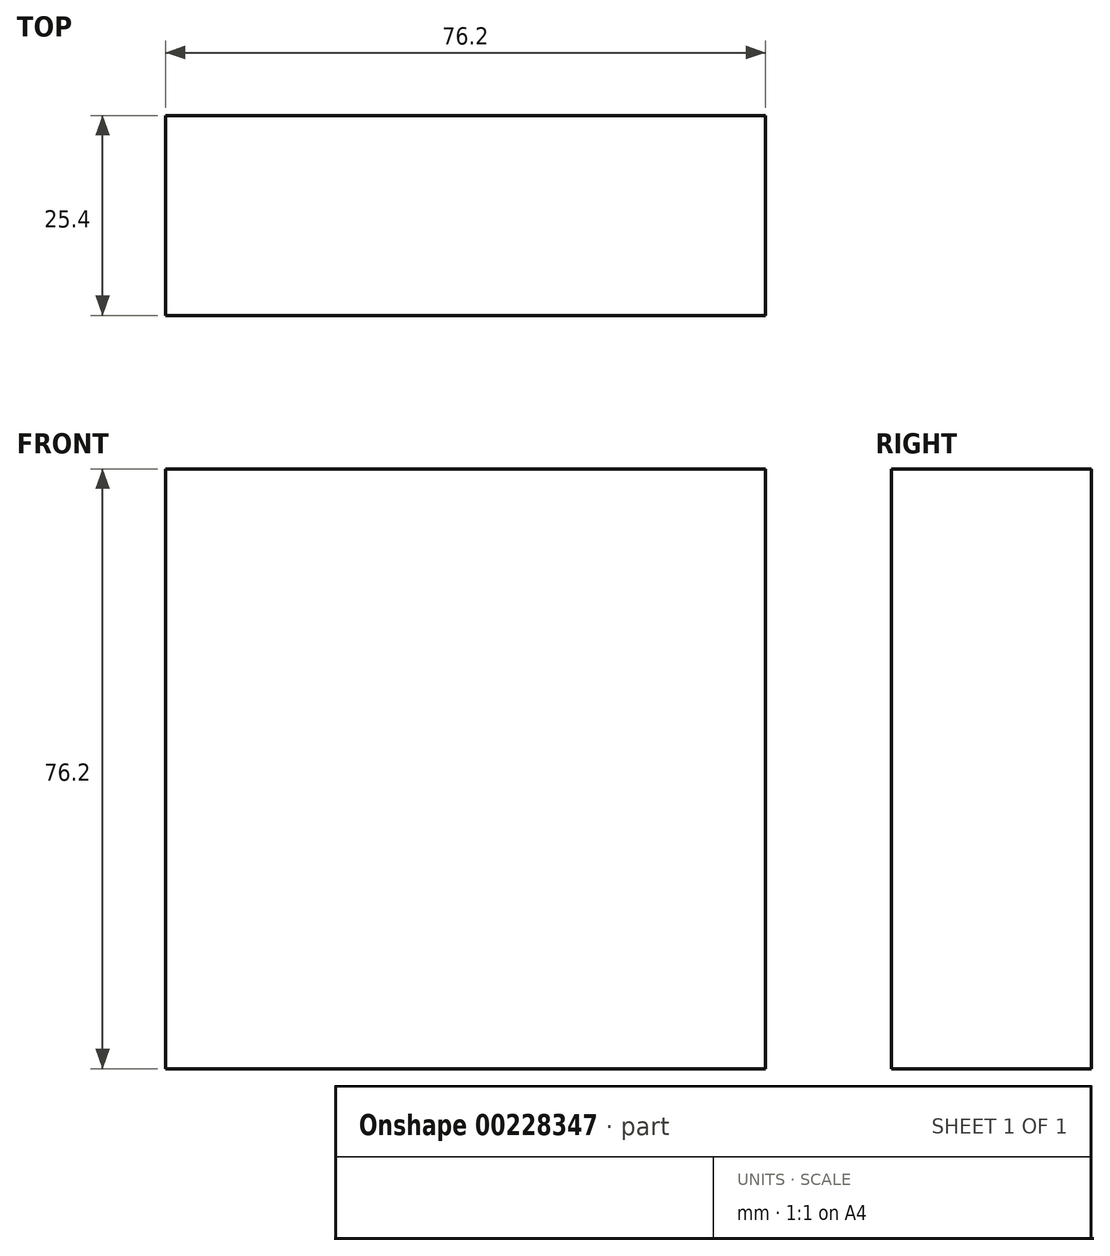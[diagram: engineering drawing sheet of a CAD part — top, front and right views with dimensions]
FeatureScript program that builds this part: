
annotation { "Feature Type Name" : "Feature", "Feature Type Description" : "" }
export const myFeature = defineFeature(function(context is Context, id is Id, definition is map)
    precondition{}
    {
        {
            var Q0;
            Q0=qCreatedBy(makeId("Front.planeOp"),FACE);
            var sketch = newSketch(context, id + "F0", { "sketchPlane" : qUnion([Q0])});
            skLineSegment(sketch, "E0.bottom", {"start": v(38.1, -38.1) * mm, "end": v(-38.1, -38.1) * mm});
            skLineSegment(sketch, "E0.top", {"start": v(38.1, 38.1) * mm, "end": v(-38.1, 38.1) * mm});
            skLineSegment(sketch, "E0.left", {"start": v(38.1, -38.1) * mm, "end": v(38.1, 38.1) * mm});
            skLineSegment(sketch, "E0.right", {"start": v(-38.1, -38.1) * mm, "end": v(-38.1, 38.1) * mm});
            skPoint(sketch, "E0.middle", {"position": v(0, 0) * mm});
            skSolve(sketch);
        }
        {
            var Q0;
            Q0=makeQuery(id+"F0.imprint","IMPRINT",FACE,{"disambiguationData":[TD([[makeQuery(id+"F0.imprint","IMPRINT",EDGE,{"derivedFrom":sQuery(id+"F0.wireOp",EDGE,"E0.bottom")}),-1.0]])]});
            extrude(context, id + "F1", {"entities" : qUnion([Q0]), "depth" : 25.4 * mm});
        }
    });
